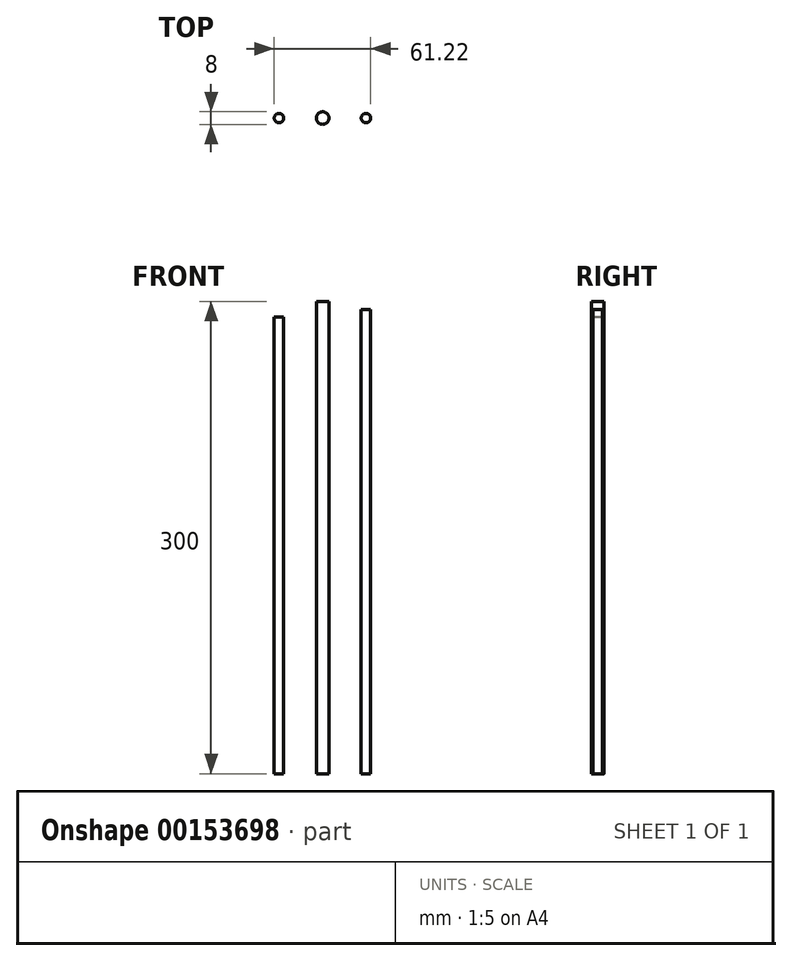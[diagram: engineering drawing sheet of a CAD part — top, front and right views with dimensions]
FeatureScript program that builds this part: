
annotation { "Feature Type Name" : "Feature", "Feature Type Description" : "" }
export const myFeature = defineFeature(function(context is Context, id is Id, definition is map)
    precondition{}
    {
        {
            var Q0;
            Q0=qCreatedBy(makeId("Top.planeOp"),FACE);
            var sketch = newSketch(context, id + "F0", { "sketchPlane" : qUnion([Q0])});
            skCircle(sketch, "E0", {"center": v(0, 0) * mm, "radius": 4 * mm});
            skCircle(sketch, "E1", {"center": v(-27.77, 0) * mm, "radius": 3 * mm});
            skCircle(sketch, "E2", {"center": v(27.45, 0) * mm, "radius": 3 * mm});
            skSolve(sketch);
        }
        {
            var Q0;
            Q0=makeQuery(id+"F0.imprint","IMPRINT",FACE,{"disambiguationData":[TD([[makeQuery(id+"F0.imprint","IMPRINT",EDGE,{"derivedFrom":sQuery(id+"F0.wireOp",EDGE,"E0")}),1.0]])]});
            extrude(context, id + "F1", {"entities" : qUnion([Q0]), "depth" : 300 * mm});
        }
        {
            var Q0;
            Q0=makeQuery(id+"F0.imprint","IMPRINT",FACE,{"disambiguationData":[TD([[makeQuery(id+"F0.imprint","IMPRINT",EDGE,{"derivedFrom":sQuery(id+"F0.wireOp",EDGE,"E1")}),1.0]])]});
            extrude(context, id + "F2", {"entities" : qUnion([Q0]), "depth" : 290 * mm});
        }
        {
            var Q0;
            Q0=makeQuery(id+"F0.imprint","IMPRINT",FACE,{"disambiguationData":[TD([[makeQuery(id+"F0.imprint","IMPRINT",EDGE,{"derivedFrom":sQuery(id+"F0.wireOp",EDGE,"E2")}),1.0]])]});
            extrude(context, id + "F3", {"entities" : qUnion([Q0]), "depth" : 295 * mm});
        }
    });
